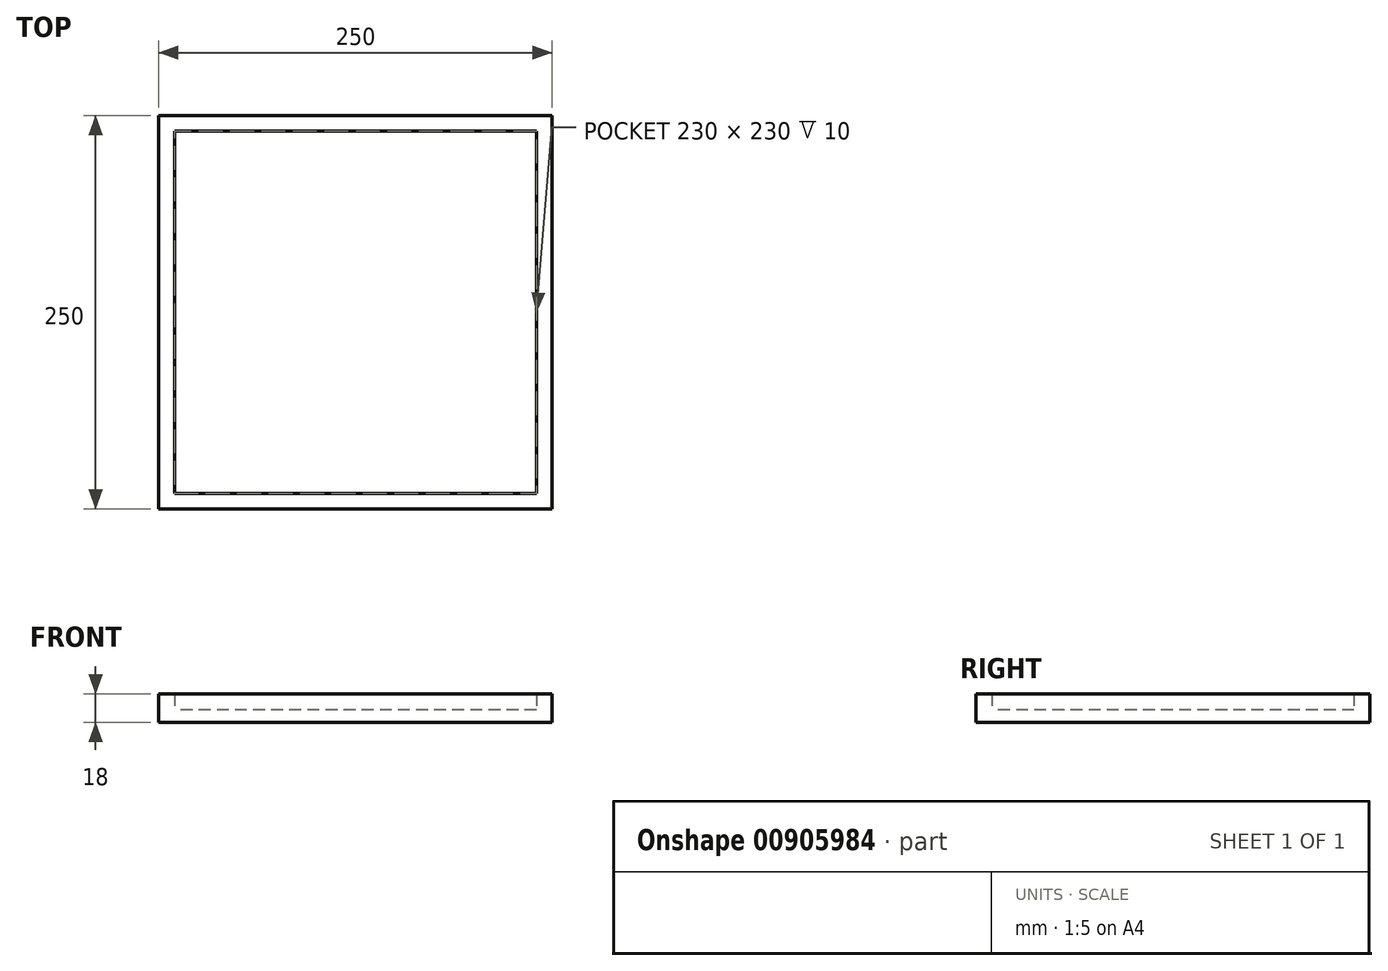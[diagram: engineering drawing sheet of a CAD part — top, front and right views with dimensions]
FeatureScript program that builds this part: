
annotation { "Feature Type Name" : "Feature", "Feature Type Description" : "" }
export const myFeature = defineFeature(function(context is Context, id is Id, definition is map)
    precondition{}
    {
        {
            var Q0;
            Q0=qCreatedBy(makeId("Top.planeOp"),FACE);
            var sketch = newSketch(context, id + "F0", { "sketchPlane" : qUnion([Q0])});
            skLineSegment(sketch, "E0.bottom", {"start": v(125, -125) * mm, "end": v(-125, -125) * mm});
            skLineSegment(sketch, "E0.top", {"start": v(125, 125) * mm, "end": v(-125, 125) * mm});
            skLineSegment(sketch, "E0.left", {"start": v(125, -125) * mm, "end": v(125, 125) * mm});
            skLineSegment(sketch, "E0.right", {"start": v(-125, -125) * mm, "end": v(-125, 125) * mm});
            skPoint(sketch, "E0.middle", {"position": v(0, 0) * mm});
            skSolve(sketch);
        }
        {
            var Q0;
            Q0=makeQuery(id+"F0.imprint","IMPRINT",FACE,{"disambiguationData":[TD([[makeQuery(id+"F0.imprint","IMPRINT",EDGE,{"derivedFrom":sQuery(id+"F0.wireOp",EDGE,"E0.bottom")}),-1.0]])]});
            extrude(context, id + "F1", {"entities" : qUnion([Q0]), "depth" : 8 * mm, "offsetDistance" : 25 * mm});
        }
        {
            var Q0;
            Q0=makeQuery(id+"F1.opExtrude","CAP_FACE",FACE,{"disambiguationData":[OSD([sQuery(id+"F0.wireOp",EDGE,"E0.bottom"),sQuery(id+"F0.wireOp",EDGE,"E0.top"),sQuery(id+"F0.wireOp",EDGE,"E0.left"),sQuery(id+"F0.wireOp",EDGE,"E0.right")])],"isStart":false});
            var sketch = newSketch(context, id + "F2", { "sketchPlane" : qUnion([Q0])});
            skLineSegment(sketch, "E1.bottom", {"start": v(115, 115) * mm, "end": v(-115, 115) * mm});
            skLineSegment(sketch, "E1.top", {"start": v(115, -115) * mm, "end": v(-115, -115) * mm});
            skLineSegment(sketch, "E1.left", {"start": v(115, 115) * mm, "end": v(115, -115) * mm});
            skLineSegment(sketch, "E1.right", {"start": v(-115, 115) * mm, "end": v(-115, -115) * mm});
            skPoint(sketch, "E1.middle", {"position": v(0, 0) * mm});
            skLineSegment(sketch, "E2.bottom", {"start": v(125, 125) * mm, "end": v(-125, 125) * mm});
            skLineSegment(sketch, "E2.top", {"start": v(125, -125) * mm, "end": v(-125, -125) * mm});
            skLineSegment(sketch, "E2.left", {"start": v(125, 125) * mm, "end": v(125, -125) * mm});
            skLineSegment(sketch, "E2.right", {"start": v(-125, 125) * mm, "end": v(-125, -125) * mm});
            skSolve(sketch);
        }
        {
            var Q0;
            Q0=makeQuery(id+"F2.imprint","IMPRINT",FACE,{"disambiguationData":[TD([[makeQuery(id+"F2.imprint","IMPRINT",EDGE,{"derivedFrom":sQuery(id+"F2.wireOp",EDGE,"E1.bottom")}),-1.0]])]});
            extrude(context, id + "F3", {"entities" : qUnion([Q0]), "operationType" : NewBodyOperationType.ADD, "depth" : 10 * mm, "offsetDistance" : 25 * mm});
        }
    });
